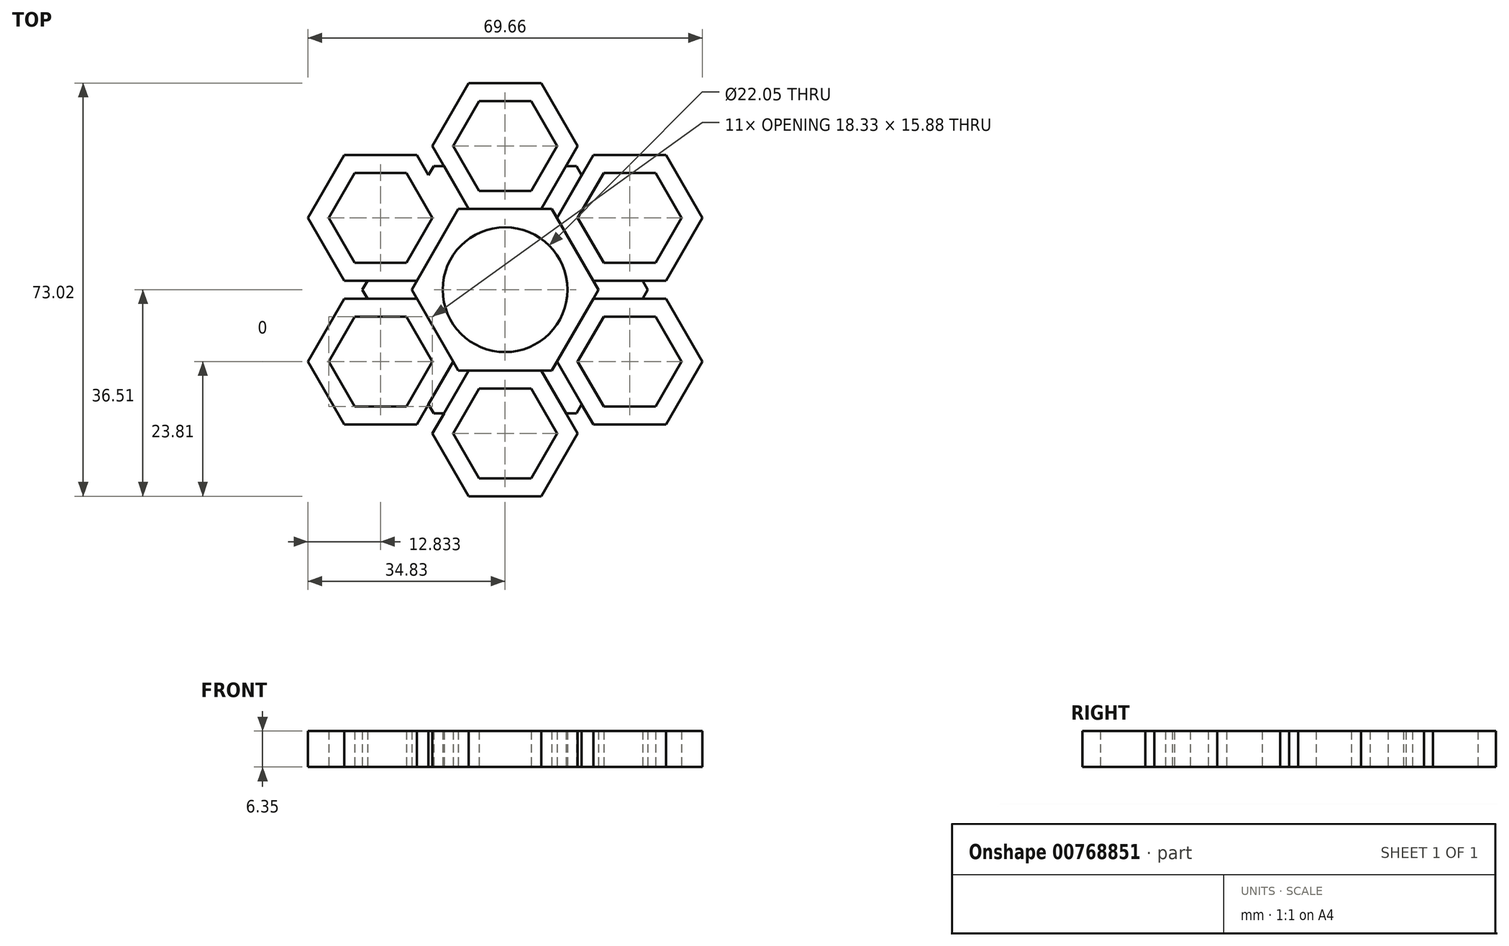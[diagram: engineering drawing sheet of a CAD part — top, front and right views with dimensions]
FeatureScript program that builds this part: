
annotation { "Feature Type Name" : "Feature", "Feature Type Description" : "" }
export const myFeature = defineFeature(function(context is Context, id is Id, definition is map)
    precondition{}
    {
        {
            var Q0;
            Q0=qCreatedBy(makeId("Top.planeOp"),FACE);
            var sketch = newSketch(context, id + "F0", { "sketchPlane" : qUnion([Q0])});
            skCircle(sketch, "E0.cCircle", {"center": v(0, 0) * mm, "radius": 14.29 * mm, "construction": true});
            skLineSegment(sketch, "E0.0", {"start": v(8.25, -14.29) * mm, "end": v(-8.25, -14.29) * mm});
            skLineSegment(sketch, "E0.1", {"start": v(-8.25, -14.29) * mm, "end": v(-16.5, 0) * mm});
            skLineSegment(sketch, "E0.2", {"start": v(-16.5, 0) * mm, "end": v(-8.25, 14.29) * mm});
            skLineSegment(sketch, "E0.3", {"start": v(-8.25, 14.29) * mm, "end": v(8.25, 14.29) * mm});
            skLineSegment(sketch, "E0.4", {"start": v(8.25, 14.29) * mm, "end": v(16.5, 0) * mm});
            skLineSegment(sketch, "E0.5", {"start": v(16.5, 0) * mm, "end": v(8.25, -14.29) * mm});
            skPoint(sketch, "E0.0.midPoint", {"position": v(0, -14.29) * mm});
            skCircle(sketch, "E1", {"center": v(0, 0) * mm, "radius": 11.02 * mm});
            skCircle(sketch, "E2.cCircle", {"center": v(0, 25.4) * mm, "radius": 11.11 * mm, "construction": true});
            skLineSegment(sketch, "E2.0", {"start": v(6.42, 14.29) * mm, "end": v(-6.42, 14.29) * mm});
            skLineSegment(sketch, "E2.1", {"start": v(-6.42, 14.29) * mm, "end": v(-12.83, 25.4) * mm});
            skLineSegment(sketch, "E2.2", {"start": v(-12.83, 25.4) * mm, "end": v(-6.42, 36.51) * mm});
            skLineSegment(sketch, "E2.3", {"start": v(-6.42, 36.51) * mm, "end": v(6.42, 36.51) * mm});
            skLineSegment(sketch, "E2.4", {"start": v(6.42, 36.51) * mm, "end": v(12.83, 25.4) * mm});
            skLineSegment(sketch, "E2.5", {"start": v(12.83, 25.4) * mm, "end": v(6.42, 14.29) * mm});
            skPoint(sketch, "E2.0.midPoint", {"position": v(0, 14.29) * mm});
            skCircle(sketch, "E3.cCircle", {"center": v(0, 25.4) * mm, "radius": 7.94 * mm, "construction": true});
            skLineSegment(sketch, "E3.0", {"start": v(4.58, 17.46) * mm, "end": v(-4.58, 17.46) * mm});
            skLineSegment(sketch, "E3.1", {"start": v(-4.58, 17.46) * mm, "end": v(-9.17, 25.4) * mm});
            skLineSegment(sketch, "E3.2", {"start": v(-9.17, 25.4) * mm, "end": v(-4.58, 33.34) * mm});
            skLineSegment(sketch, "E3.3", {"start": v(-4.58, 33.34) * mm, "end": v(4.58, 33.34) * mm});
            skLineSegment(sketch, "E3.4", {"start": v(4.58, 33.34) * mm, "end": v(9.17, 25.4) * mm});
            skLineSegment(sketch, "E3.5", {"start": v(9.17, 25.4) * mm, "end": v(4.58, 17.46) * mm});
            skPoint(sketch, "E3.0.midPoint", {"position": v(0, 17.46) * mm});
            skLineSegment(sketch, "E4.1.0", {"start": v(-34.83, 12.7) * mm, "end": v(-28.41, 23.81) * mm});
            skLineSegment(sketch, "E4.1.1", {"start": v(-31.16, 12.7) * mm, "end": v(-26.58, 20.64) * mm});
            skLineSegment(sketch, "E4.1.2", {"start": v(-26.58, 20.64) * mm, "end": v(-17.41, 20.64) * mm});
            skLineSegment(sketch, "E4.1.3", {"start": v(-28.41, 23.81) * mm, "end": v(-15.58, 23.81) * mm});
            skLineSegment(sketch, "E4.1.4", {"start": v(-15.58, 23.81) * mm, "end": v(-9.17, 12.7) * mm});
            skLineSegment(sketch, "E4.1.5", {"start": v(-17.41, 20.64) * mm, "end": v(-12.83, 12.7) * mm});
            skLineSegment(sketch, "E4.1.6", {"start": v(-17.41, 4.76) * mm, "end": v(-26.58, 4.76) * mm});
            skLineSegment(sketch, "E4.1.7", {"start": v(-26.58, 4.76) * mm, "end": v(-31.16, 12.7) * mm});
            skLineSegment(sketch, "E4.1.8", {"start": v(-12.83, 12.7) * mm, "end": v(-17.41, 4.76) * mm});
            skLineSegment(sketch, "E4.1.9", {"start": v(-15.58, 1.59) * mm, "end": v(-28.41, 1.59) * mm});
            skLineSegment(sketch, "E4.1.10", {"start": v(-28.41, 1.59) * mm, "end": v(-34.83, 12.7) * mm});
            skLineSegment(sketch, "E4.2.0", {"start": v(-28.41, -23.81) * mm, "end": v(-34.83, -12.7) * mm});
            skLineSegment(sketch, "E4.2.1", {"start": v(-26.58, -20.64) * mm, "end": v(-31.16, -12.7) * mm});
            skLineSegment(sketch, "E4.2.2", {"start": v(-31.16, -12.7) * mm, "end": v(-26.58, -4.76) * mm});
            skLineSegment(sketch, "E4.2.3", {"start": v(-34.83, -12.7) * mm, "end": v(-28.41, -1.59) * mm});
            skLineSegment(sketch, "E4.2.4", {"start": v(-28.41, -1.59) * mm, "end": v(-15.58, -1.59) * mm});
            skLineSegment(sketch, "E4.2.5", {"start": v(-26.58, -4.76) * mm, "end": v(-17.41, -4.76) * mm});
            skLineSegment(sketch, "E4.2.6", {"start": v(-12.83, -12.7) * mm, "end": v(-17.41, -20.64) * mm});
            skLineSegment(sketch, "E4.2.7", {"start": v(-17.41, -20.64) * mm, "end": v(-26.58, -20.64) * mm});
            skLineSegment(sketch, "E4.2.8", {"start": v(-17.41, -4.76) * mm, "end": v(-12.83, -12.7) * mm});
            skLineSegment(sketch, "E4.2.9", {"start": v(-9.17, -12.7) * mm, "end": v(-15.58, -23.81) * mm});
            skLineSegment(sketch, "E4.2.10", {"start": v(-15.58, -23.81) * mm, "end": v(-28.41, -23.81) * mm});
            skLineSegment(sketch, "E4.3.0", {"start": v(6.42, -36.51) * mm, "end": v(-6.42, -36.51) * mm});
            skLineSegment(sketch, "E4.3.1", {"start": v(4.58, -33.34) * mm, "end": v(-4.58, -33.34) * mm});
            skLineSegment(sketch, "E4.3.2", {"start": v(-4.58, -33.34) * mm, "end": v(-9.17, -25.4) * mm});
            skLineSegment(sketch, "E4.3.3", {"start": v(-6.42, -36.51) * mm, "end": v(-12.83, -25.4) * mm});
            skLineSegment(sketch, "E4.3.4", {"start": v(-12.83, -25.4) * mm, "end": v(-6.42, -14.29) * mm});
            skLineSegment(sketch, "E4.3.5", {"start": v(-9.17, -25.4) * mm, "end": v(-4.58, -17.46) * mm});
            skLineSegment(sketch, "E4.3.6", {"start": v(4.58, -17.46) * mm, "end": v(9.17, -25.4) * mm});
            skLineSegment(sketch, "E4.3.7", {"start": v(9.17, -25.4) * mm, "end": v(4.58, -33.34) * mm});
            skLineSegment(sketch, "E4.3.8", {"start": v(-4.58, -17.46) * mm, "end": v(4.58, -17.46) * mm});
            skLineSegment(sketch, "E4.3.9", {"start": v(6.42, -14.29) * mm, "end": v(12.83, -25.4) * mm});
            skLineSegment(sketch, "E4.3.10", {"start": v(12.83, -25.4) * mm, "end": v(6.42, -36.51) * mm});
            skLineSegment(sketch, "E4.4.0", {"start": v(34.83, -12.7) * mm, "end": v(28.41, -23.81) * mm});
            skLineSegment(sketch, "E4.4.1", {"start": v(31.16, -12.7) * mm, "end": v(26.58, -20.64) * mm});
            skLineSegment(sketch, "E4.4.2", {"start": v(26.58, -20.64) * mm, "end": v(17.41, -20.64) * mm});
            skLineSegment(sketch, "E4.4.3", {"start": v(28.41, -23.81) * mm, "end": v(15.58, -23.81) * mm});
            skLineSegment(sketch, "E4.4.4", {"start": v(15.58, -23.81) * mm, "end": v(9.17, -12.7) * mm});
            skLineSegment(sketch, "E4.4.5", {"start": v(17.41, -20.64) * mm, "end": v(12.83, -12.7) * mm});
            skLineSegment(sketch, "E4.4.6", {"start": v(17.41, -4.76) * mm, "end": v(26.58, -4.76) * mm});
            skLineSegment(sketch, "E4.4.7", {"start": v(26.58, -4.76) * mm, "end": v(31.16, -12.7) * mm});
            skLineSegment(sketch, "E4.4.8", {"start": v(12.83, -12.7) * mm, "end": v(17.41, -4.76) * mm});
            skLineSegment(sketch, "E4.4.9", {"start": v(15.58, -1.59) * mm, "end": v(28.41, -1.59) * mm});
            skLineSegment(sketch, "E4.4.10", {"start": v(28.41, -1.59) * mm, "end": v(34.83, -12.7) * mm});
            skLineSegment(sketch, "E4.5.0", {"start": v(28.41, 23.81) * mm, "end": v(34.83, 12.7) * mm});
            skLineSegment(sketch, "E4.5.1", {"start": v(26.58, 20.64) * mm, "end": v(31.16, 12.7) * mm});
            skLineSegment(sketch, "E4.5.2", {"start": v(31.16, 12.7) * mm, "end": v(26.58, 4.76) * mm});
            skLineSegment(sketch, "E4.5.3", {"start": v(34.83, 12.7) * mm, "end": v(28.41, 1.59) * mm});
            skLineSegment(sketch, "E4.5.4", {"start": v(28.41, 1.59) * mm, "end": v(15.58, 1.59) * mm});
            skLineSegment(sketch, "E4.5.5", {"start": v(26.58, 4.76) * mm, "end": v(17.41, 4.76) * mm});
            skLineSegment(sketch, "E4.5.6", {"start": v(12.83, 12.7) * mm, "end": v(17.41, 20.64) * mm});
            skLineSegment(sketch, "E4.5.7", {"start": v(17.41, 20.64) * mm, "end": v(26.58, 20.64) * mm});
            skLineSegment(sketch, "E4.5.8", {"start": v(17.41, 4.76) * mm, "end": v(12.83, 12.7) * mm});
            skLineSegment(sketch, "E4.5.9", {"start": v(9.17, 12.7) * mm, "end": v(15.58, 23.81) * mm});
            skLineSegment(sketch, "E4.5.10", {"start": v(15.58, 23.81) * mm, "end": v(28.41, 23.81) * mm});
            skSolve(sketch);
        }
        {
            var Q0;
            Q0=qCreatedBy(makeId("Top.planeOp"),FACE);
            var sketch = newSketch(context, id + "F1", { "sketchPlane" : qUnion([Q0])});
            skLineSegment(sketch, "E5.0", {"start": v(-4.58, 33.34) * mm, "end": v(4.58, 33.34) * mm});
            skLineSegment(sketch, "E5.1", {"start": v(26.58, 20.64) * mm, "end": v(31.16, 12.7) * mm});
            skLineSegment(sketch, "E5.2", {"start": v(9.17, -25.4) * mm, "end": v(4.58, -33.34) * mm});
            skLineSegment(sketch, "E5.3", {"start": v(-31.16, -12.7) * mm, "end": v(-26.58, -4.76) * mm});
            skLineSegment(sketch, "E5.4", {"start": v(4.58, 33.34) * mm, "end": v(9.17, 25.4) * mm});
            skLineSegment(sketch, "E5.5", {"start": v(31.16, 12.7) * mm, "end": v(26.58, 4.76) * mm});
            skLineSegment(sketch, "E5.6", {"start": v(-4.58, -17.46) * mm, "end": v(4.58, -17.46) * mm});
            skLineSegment(sketch, "E5.7", {"start": v(-34.83, -12.7) * mm, "end": v(-28.41, -1.59) * mm});
            skLineSegment(sketch, "E5.8", {"start": v(9.17, 25.4) * mm, "end": v(4.58, 17.46) * mm});
            skLineSegment(sketch, "E5.9", {"start": v(34.83, 12.7) * mm, "end": v(28.41, 1.59) * mm});
            skLineSegment(sketch, "E5.10", {"start": v(6.42, -14.29) * mm, "end": v(12.83, -25.4) * mm});
            skLineSegment(sketch, "E5.11", {"start": v(-28.41, -1.59) * mm, "end": v(-15.58, -1.59) * mm});
            skLineSegment(sketch, "E5.12", {"start": v(-34.83, 12.7) * mm, "end": v(-28.41, 23.81) * mm});
            skLineSegment(sketch, "E5.13", {"start": v(28.41, 1.59) * mm, "end": v(15.58, 1.59) * mm});
            skLineSegment(sketch, "E5.14", {"start": v(12.83, -25.4) * mm, "end": v(6.42, -36.51) * mm});
            skLineSegment(sketch, "E5.15", {"start": v(-26.58, -4.76) * mm, "end": v(-17.41, -4.76) * mm});
            skLineSegment(sketch, "E5.16", {"start": v(34.83, -12.7) * mm, "end": v(28.41, -23.81) * mm});
            skLineSegment(sketch, "E5.17", {"start": v(-12.83, -12.7) * mm, "end": v(-17.41, -20.64) * mm});
            skLineSegment(sketch, "E5.18", {"start": v(-31.16, 12.7) * mm, "end": v(-26.58, 20.64) * mm});
            skLineSegment(sketch, "E5.19", {"start": v(26.58, 4.76) * mm, "end": v(17.41, 4.76) * mm});
            skLineSegment(sketch, "E5.20", {"start": v(31.16, -12.7) * mm, "end": v(26.58, -20.64) * mm});
            skLineSegment(sketch, "E5.21", {"start": v(-17.41, -20.64) * mm, "end": v(-26.58, -20.64) * mm});
            skLineSegment(sketch, "E5.22", {"start": v(-26.58, 20.64) * mm, "end": v(-17.41, 20.64) * mm});
            skLineSegment(sketch, "E5.23", {"start": v(12.83, 12.7) * mm, "end": v(17.41, 20.64) * mm});
            skLineSegment(sketch, "E5.24", {"start": v(26.58, -20.64) * mm, "end": v(17.41, -20.64) * mm});
            skLineSegment(sketch, "E5.25", {"start": v(-17.41, -4.76) * mm, "end": v(-12.83, -12.7) * mm});
            skLineSegment(sketch, "E5.26", {"start": v(-28.41, 23.81) * mm, "end": v(-15.58, 23.81) * mm});
            skLineSegment(sketch, "E5.27", {"start": v(17.41, 20.64) * mm, "end": v(26.58, 20.64) * mm});
            skLineSegment(sketch, "E5.28", {"start": v(28.41, -23.81) * mm, "end": v(15.58, -23.81) * mm});
            skLineSegment(sketch, "E5.29", {"start": v(-9.17, -12.7) * mm, "end": v(-15.58, -23.81) * mm});
            skLineSegment(sketch, "E5.30", {"start": v(-15.58, 23.81) * mm, "end": v(-9.17, 12.7) * mm});
            skLineSegment(sketch, "E5.31", {"start": v(17.41, 4.76) * mm, "end": v(12.83, 12.7) * mm});
            skLineSegment(sketch, "E5.32", {"start": v(15.58, -23.81) * mm, "end": v(9.17, -12.7) * mm});
            skLineSegment(sketch, "E5.33", {"start": v(-15.58, -23.81) * mm, "end": v(-28.41, -23.81) * mm});
            skLineSegment(sketch, "E5.34", {"start": v(-17.41, 20.64) * mm, "end": v(-12.83, 12.7) * mm});
            skLineSegment(sketch, "E5.35", {"start": v(9.17, 12.7) * mm, "end": v(15.58, 23.81) * mm});
            skLineSegment(sketch, "E5.36", {"start": v(17.41, -4.76) * mm, "end": v(26.58, -4.76) * mm});
            skLineSegment(sketch, "E5.37", {"start": v(4.58, -33.34) * mm, "end": v(-4.58, -33.34) * mm});
            skLineSegment(sketch, "E5.38", {"start": v(-26.58, 4.76) * mm, "end": v(-31.16, 12.7) * mm});
            skLineSegment(sketch, "E5.39", {"start": v(17.41, -20.64) * mm, "end": v(12.83, -12.7) * mm});
            skLineSegment(sketch, "E5.40", {"start": v(6.42, -36.51) * mm, "end": v(-6.42, -36.51) * mm});
            skLineSegment(sketch, "E5.41", {"start": v(-17.41, 4.76) * mm, "end": v(-26.58, 4.76) * mm});
            skLineSegment(sketch, "E5.42", {"start": v(15.58, 23.81) * mm, "end": v(28.41, 23.81) * mm});
            skLineSegment(sketch, "E5.43", {"start": v(26.58, -4.76) * mm, "end": v(31.16, -12.7) * mm});
            skLineSegment(sketch, "E5.44", {"start": v(-4.58, -33.34) * mm, "end": v(-9.17, -25.4) * mm});
            skLineSegment(sketch, "E5.45", {"start": v(-12.83, 12.7) * mm, "end": v(-17.41, 4.76) * mm});
            skLineSegment(sketch, "E5.46", {"start": v(12.83, -12.7) * mm, "end": v(17.41, -4.76) * mm});
            skLineSegment(sketch, "E5.47", {"start": v(-6.42, -36.51) * mm, "end": v(-12.83, -25.4) * mm});
            skLineSegment(sketch, "E5.48", {"start": v(-15.58, 1.59) * mm, "end": v(-28.41, 1.59) * mm});
            skLineSegment(sketch, "E5.49", {"start": v(6.42, 36.51) * mm, "end": v(12.83, 25.4) * mm});
            skLineSegment(sketch, "E5.50", {"start": v(12.83, 25.4) * mm, "end": v(6.42, 14.29) * mm});
            skCircle(sketch, "E5.51", {"center": v(0, 25.4) * mm, "radius": 7.94 * mm});
            skLineSegment(sketch, "E5.53", {"start": v(8.25, -14.29) * mm, "end": v(-8.25, -14.29) * mm});
            skLineSegment(sketch, "E5.54", {"start": v(-8.25, -14.29) * mm, "end": v(-16.5, 0) * mm});
            skLineSegment(sketch, "E5.55", {"start": v(-16.5, 0) * mm, "end": v(-8.25, 14.29) * mm});
            skLineSegment(sketch, "E5.56", {"start": v(8.25, 14.29) * mm, "end": v(16.5, 0) * mm});
            skLineSegment(sketch, "E5.57", {"start": v(16.5, 0) * mm, "end": v(8.25, -14.29) * mm});
            skCircle(sketch, "E5.58", {"center": v(0, 0) * mm, "radius": 11.02 * mm});
            skCircle(sketch, "E5.59", {"center": v(0, 25.4) * mm, "radius": 11.11 * mm});
            skLineSegment(sketch, "E5.60", {"start": v(6.42, 14.29) * mm, "end": v(-6.42, 14.29) * mm});
            skLineSegment(sketch, "E5.61", {"start": v(-6.42, 14.29) * mm, "end": v(-12.83, 25.4) * mm});
            skLineSegment(sketch, "E5.62", {"start": v(-12.83, 25.4) * mm, "end": v(-6.42, 36.51) * mm});
            skLineSegment(sketch, "E5.63", {"start": v(-6.42, 36.51) * mm, "end": v(6.42, 36.51) * mm});
            skLineSegment(sketch, "E5.64", {"start": v(4.58, 17.46) * mm, "end": v(-4.58, 17.46) * mm});
            skLineSegment(sketch, "E5.65", {"start": v(15.58, -1.59) * mm, "end": v(28.41, -1.59) * mm});
            skLineSegment(sketch, "E5.66", {"start": v(-12.83, -25.4) * mm, "end": v(-6.42, -14.29) * mm});
            skLineSegment(sketch, "E5.67", {"start": v(-28.41, 1.59) * mm, "end": v(-34.83, 12.7) * mm});
            skLineSegment(sketch, "E5.68", {"start": v(-4.58, 17.46) * mm, "end": v(-9.17, 25.4) * mm});
            skLineSegment(sketch, "E5.69", {"start": v(28.41, -1.59) * mm, "end": v(34.83, -12.7) * mm});
            skLineSegment(sketch, "E5.70", {"start": v(-9.17, -25.4) * mm, "end": v(-4.58, -17.46) * mm});
            skLineSegment(sketch, "E5.71", {"start": v(-28.41, -23.81) * mm, "end": v(-34.83, -12.7) * mm});
            skLineSegment(sketch, "E5.72", {"start": v(-9.17, 25.4) * mm, "end": v(-4.58, 33.34) * mm});
            skLineSegment(sketch, "E5.73", {"start": v(28.41, 23.81) * mm, "end": v(34.83, 12.7) * mm});
            skLineSegment(sketch, "E5.74", {"start": v(4.58, -17.46) * mm, "end": v(9.17, -25.4) * mm});
            skLineSegment(sketch, "E5.75", {"start": v(-26.58, -20.64) * mm, "end": v(-31.16, -12.7) * mm});
            skCircle(sketch, "E6.cCircle", {"center": v(-11.69, 20.24) * mm, "radius": 1.59 * mm, "construction": true});
            skLineSegment(sketch, "E6.0", {"start": v(-9.85, 20.24) * mm, "end": v(-10.77, 18.65) * mm});
            skLineSegment(sketch, "E6.1", {"start": v(-10.77, 18.65) * mm, "end": v(-12.6, 18.65) * mm});
            skLineSegment(sketch, "E6.2", {"start": v(-12.6, 18.65) * mm, "end": v(-13.52, 20.24) * mm});
            skLineSegment(sketch, "E6.3", {"start": v(-13.52, 20.24) * mm, "end": v(-12.6, 21.83) * mm});
            skLineSegment(sketch, "E6.4", {"start": v(-12.6, 21.83) * mm, "end": v(-10.77, 21.83) * mm});
            skLineSegment(sketch, "E6.5", {"start": v(-10.77, 21.83) * mm, "end": v(-9.85, 20.24) * mm});
            skPoint(sketch, "E6.0.midPoint", {"position": v(-10.31, 19.45) * mm});
            skPoint(sketch, "E7.trimOffspring.end.orphan", {"position": v(-9.62, 19.84) * mm});
            skPoint(sketch, "E8.start.orphan", {"position": v(-12.37, 18.26) * mm});
            skLineSegment(sketch, "E9", {"start": v(-8.25, 14.29) * mm, "end": v(-6.42, 14.29) * mm});
            skSolve(sketch);
        }
        {
            var Q0;
            Q0=makeQuery(id+"F1.imprint","IMPRINT",FACE,{"disambiguationData":[TD([[makeQuery(id+"F1.imprint","IMPRINT",EDGE,{"derivedFrom":sQuery(id+"F1.wireOp",EDGE,"E6.0")}),-1.0]])]});
            var Q1;
            Q1=makeQuery(id+"F0.imprint","IMPRINT",FACE,{"disambiguationData":[TD([[makeQuery(id+"F0.imprint","IMPRINT",EDGE,{"derivedFrom":sQuery(id+"F0.wireOp",EDGE,"E1")}),-1.0]])]});
            var Q2;
            Q2=makeQuery(id+"F1.imprint","IMPRINT",FACE,{"disambiguationData":[TD([[makeQuery(id+"F1.imprint","IMPRINT",EDGE,{"derivedFrom":sQuery(id+"F1.wireOp",EDGE,"E5.12")}),-1.0]])]});
            var Q3;
            {var subQ1=sQuery(id+"F0.wireOp",EDGE,"E2.1");Q3=makeQuery(id+"F0.imprint","IMPRINT",FACE,{"disambiguationData":[TD([[makeQuery(id+"F0.imprint","IMPRINT",EDGE,{"derivedFrom":subQ1}),-1.0]])]});}
            var Q4;
            {var subQ7=sQuery(id+"F1.wireOp",EDGE,"E6.0");Q4=makeQuery(id+"F1.imprint","IMPRINT",FACE,{"disambiguationData":[TD([[makeQuery(id+"F1.imprint","IMPRINT",EDGE,{"derivedFrom":subQ7}),1.0]])]});}
            var Q5;
            Q5=makeQuery(id+"F1.imprint","IMPRINT",FACE,{"disambiguationData":[TD([[makeQuery(id+"F1.imprint","IMPRINT",EDGE,{"derivedFrom":sQuery(id+"F1.wireOp",EDGE,"E5.1")}),1.0]])]});
            var Q6;
            Q6=makeQuery(id+"F0.imprint","IMPRINT",FACE,{"disambiguationData":[TD([[makeQuery(id+"F0.imprint","IMPRINT",EDGE,{"derivedFrom":sQuery(id+"F0.wireOp",EDGE,"E4.4.0")}),-1.0]])]});
            var Q7;
            Q7=makeQuery(id+"F0.imprint","IMPRINT",FACE,{"disambiguationData":[TD([[makeQuery(id+"F0.imprint","IMPRINT",EDGE,{"derivedFrom":sQuery(id+"F0.wireOp",EDGE,"E4.3.0")}),-1.0]])]});
            var Q8;
            Q8=makeQuery(id+"F0.imprint","IMPRINT",FACE,{"disambiguationData":[TD([[makeQuery(id+"F0.imprint","IMPRINT",EDGE,{"derivedFrom":sQuery(id+"F0.wireOp",EDGE,"E4.2.0")}),-1.0]])]});
            extrude(context, id + "F2", {"entities" : qUnion([Q0, Q1, Q2, Q3, Q4, Q5, Q6, Q7, Q8]), "depth" : 6.35 * mm, "offsetDistance" : 25.4 * mm});
        }
        {
            var Q0;
            Q0=makeQuery(id+"F2.opExtrude","SWEPT_BODY",BODY,{"disambiguationData":[OSD([sQuery(id+"F1.wireOp",EDGE,"E5.12"),sQuery(id+"F1.wireOp",EDGE,"E5.18"),sQuery(id+"F1.wireOp",EDGE,"E5.22"),sQuery(id+"F1.wireOp",EDGE,"E5.26"),sQuery(id+"F1.wireOp",EDGE,"E5.30"),sQuery(id+"F1.wireOp",EDGE,"E5.34"),sQuery(id+"F1.wireOp",EDGE,"E5.38"),sQuery(id+"F1.wireOp",EDGE,"E5.41"),sQuery(id+"F1.wireOp",EDGE,"E5.45"),sQuery(id+"F1.wireOp",EDGE,"E5.48"),sQuery(id+"F1.wireOp",EDGE,"E5.55"),sQuery(id+"F1.wireOp",EDGE,"E5.61"),sQuery(id+"F1.wireOp",EDGE,"E5.67"),sQuery(id+"F1.wireOp",EDGE,"E6.3"),sQuery(id+"F1.wireOp",EDGE,"E6.4"),sQuery(id+"F1.wireOp",EDGE,"E6.5"),sQuery(id+"F1.wireOp",EDGE,"E9")])]});
            var Q1;
            Q1=makeQuery(id+"F2.opExtrude","CAP_EDGE",EDGE,{"disambiguationData":[OSD([sQuery(id+"F0.wireOp",EDGE,"E1")])],"isStart":false});
            circularPattern(context, id + "F3", {"entities" : qUnion([Q0]), "axis" : qUnion([Q1]), "angle" : 360 * degree, "instanceCount" : 6, "equalSpace" : true});
        }
    });
